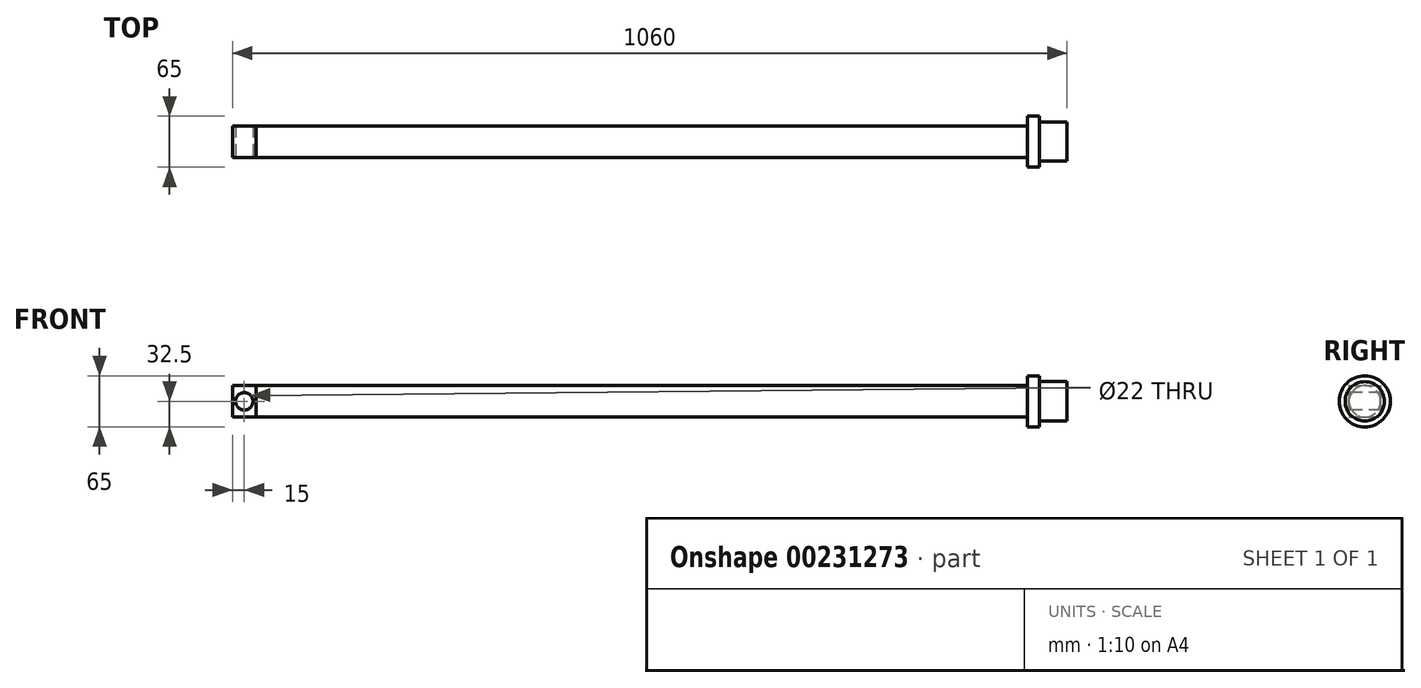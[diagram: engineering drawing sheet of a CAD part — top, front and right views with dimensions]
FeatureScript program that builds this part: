
annotation { "Feature Type Name" : "Feature", "Feature Type Description" : "" }
export const myFeature = defineFeature(function(context is Context, id is Id, definition is map)
    precondition{}
    {
        {
            var Q0;
            Q0=qCreatedBy(makeId("Right.planeOp"),FACE);
            var sketch = newSketch(context, id + "F0", { "sketchPlane" : qUnion([Q0])});
            skCircle(sketch, "E0", {"center": v(0, 0) * mm, "radius": 20 * mm});
            skSolve(sketch);
        }
        {
            var Q0;
            Q0=makeQuery(id+"F0.imprint","IMPRINT",FACE,{"disambiguationData":[TD([[makeQuery(id+"F0.imprint","IMPRINT",EDGE,{"derivedFrom":sQuery(id+"F0.wireOp",EDGE,"E0")}),1.0]])]});
            extrude(context, id + "F1", {"entities" : qUnion([Q0]), "endBound" : BoundingType.SYMMETRIC, "depth" : 1010 * mm});
        }
        {
            var Q0;
            Q0=makeQuery(id+"F1.opExtrude","CAP_FACE",FACE,{"disambiguationData":[OSD([sQuery(id+"F0.wireOp",EDGE,"E0")])],"isStart":false});
            var sketch = newSketch(context, id + "F2", { "sketchPlane" : qUnion([Q0])});
            skCircle(sketch, "E1", {"center": v(0, 0) * mm, "radius": 32.5 * mm});
            skCircle(sketch, "E2", {"center": v(0, 0) * mm, "radius": 25 * mm});
            skSolve(sketch);
        }
        {
            var Q0;
            Q0=makeQuery(id+"F2.imprint","IMPRINT",FACE,{"disambiguationData":[TD([[makeQuery(id+"F2.imprint","IMPRINT",EDGE,{"derivedFrom":sQuery(id+"F2.wireOp",EDGE,"E2")}),1.0]])]});
            var Q1;
            Q1=makeQuery(id+"F1.opExtrude","CAP_FACE",FACE,{"disambiguationData":[OSD([sQuery(id+"F0.wireOp",EDGE,"E0")])],"isStart":false});
            extrude(context, id + "F3", {"entities" : qUnion([Q0, Q1]), "operationType" : NewBodyOperationType.ADD, "depth" : 50 * mm});
        }
        {
            var Q0;
            Q0=makeQuery(id+"F2.imprint","IMPRINT",FACE,{"disambiguationData":[TD([[makeQuery(id+"F2.imprint","IMPRINT",EDGE,{"derivedFrom":sQuery(id+"F2.wireOp",EDGE,"E1")}),1.0]])]});
            extrude(context, id + "F4", {"entities" : qUnion([Q0]), "operationType" : NewBodyOperationType.ADD, "depth" : 15 * mm});
        }
        {
            var Q0;
            Q0=qCreatedBy(makeId("Front.planeOp"),FACE);
            var sketch = newSketch(context, id + "F5", { "sketchPlane" : qUnion([Q0])});
            skLineSegment(sketch, "E3", {"start": v(0, 0) * mm, "end": v(-517.62, 0) * mm, "construction": true});
            skLineSegment(sketch, "E4.0", {"start": v(-505, 20) * mm, "end": v(-505, -20) * mm, "construction": true});
            skCircle(sketch, "E5", {"center": v(-490, 0) * mm, "radius": 11 * mm});
            skSolve(sketch);
        }
        {
            var Q0;
            Q0=makeQuery(id+"F5.imprint","IMPRINT",FACE,{"disambiguationData":[TD([[makeQuery(id+"F5.imprint","IMPRINT",EDGE,{"derivedFrom":sQuery(id+"F5.wireOp",EDGE,"E5")}),1.0]])]});
            extrude(context, id + "F6", {"entities" : qUnion([Q0]), "operationType" : NewBodyOperationType.REMOVE, "endBound" : BoundingType.THROUGH_ALL, "oppositeDirection" : true, "depth" : 25 * mm, "hasSecondDirection" : true, "secondDirectionOppositeDirection" : false, "secondDirectionDepth" : 25 * mm});
        }
        {
            var Q0;
            Q0=makeQuery(id+"F1.opExtrude","CAP_FACE",FACE,{"disambiguationData":[OSD([sQuery(id+"F0.wireOp",EDGE,"E0")])],"isStart":true});
            var sketch = newSketch(context, id + "F7", { "sketchPlane" : qUnion([Q0])});
            skLineSegment(sketch, "E6.bottom", {"start": v(20, 20) * mm, "end": v(-20, 20) * mm});
            skLineSegment(sketch, "E6.top", {"start": v(20, -20) * mm, "end": v(-20, -20) * mm});
            skLineSegment(sketch, "E6.left", {"start": v(20, 20) * mm, "end": v(20, -20) * mm});
            skLineSegment(sketch, "E6.right", {"start": v(-20, 20) * mm, "end": v(-20, -20) * mm});
            skPoint(sketch, "E6.middle", {"position": v(0, 0) * mm});
            skCircle(sketch, "E7.0.0", {"center": v(0, 0) * mm, "radius": 20 * mm});
            skSolve(sketch);
        }
        {
            var Q0;
            {var subQ0=sQuery(id+"F7.wireOp",EDGE,"E6.right");var subQ1=sQuery(id+"F7.wireOp",EDGE,"E6.bottom");var subQ2=makeQuery(id+"F7.imprint","INTERSECT",VERTEX,{"derivedFrom":[subQ1,subQ0]});Q0=makeQuery(id+"F7.imprint","IMPRINT",FACE,{"disambiguationData":[TD([[makeQuery(id+"F7.imprint","IMPRINT",EDGE,{"disambiguationData":[TD([[subQ2,1.0]])],"derivedFrom":subQ1}),1.0]])]});}
            var Q1;
            {var subQ0=sQuery(id+"F7.wireOp",EDGE,"E6.right");var subQ1=sQuery(id+"F7.wireOp",EDGE,"E6.top");var subQ2=makeQuery(id+"F7.imprint","INTERSECT",VERTEX,{"derivedFrom":[subQ1,subQ0]});Q1=makeQuery(id+"F7.imprint","IMPRINT",FACE,{"disambiguationData":[TD([[makeQuery(id+"F7.imprint","IMPRINT",EDGE,{"disambiguationData":[TD([[subQ2,1.0]])],"derivedFrom":subQ1}),-1.0]])]});}
            var Q2;
            {var subQ0=sQuery(id+"F7.wireOp",EDGE,"E6.left");var subQ1=sQuery(id+"F7.wireOp",EDGE,"E6.top");var subQ2=makeQuery(id+"F7.imprint","INTERSECT",VERTEX,{"derivedFrom":[subQ1,subQ0]});Q2=makeQuery(id+"F7.imprint","IMPRINT",FACE,{"disambiguationData":[TD([[makeQuery(id+"F7.imprint","IMPRINT",EDGE,{"disambiguationData":[TD([[subQ2,-1.0]])],"derivedFrom":subQ1}),-1.0]])]});}
            var Q3;
            {var subQ0=sQuery(id+"F7.wireOp",EDGE,"E6.left");var subQ1=sQuery(id+"F7.wireOp",EDGE,"E6.bottom");var subQ2=makeQuery(id+"F7.imprint","INTERSECT",VERTEX,{"derivedFrom":[subQ1,subQ0]});Q3=makeQuery(id+"F7.imprint","IMPRINT",FACE,{"disambiguationData":[TD([[makeQuery(id+"F7.imprint","IMPRINT",EDGE,{"disambiguationData":[TD([[subQ2,-1.0]])],"derivedFrom":subQ1}),1.0]])]});}
            var Q4;
            {var subQ0=sQuery(id+"F7.wireOp",EDGE,"E7.0.0");var subQ1=makeQuery(id+"F7.imprint","INTERSECT",VERTEX,{"derivedFrom":[sQuery(id+"F7.wireOp",EDGE,"E6.bottom"),subQ0]});Q4=makeQuery(id+"F7.imprint","IMPRINT",FACE,{"disambiguationData":[TD([[makeQuery(id+"F7.imprint","IMPRINT",EDGE,{"disambiguationData":[TD([[subQ1,1.0]])],"derivedFrom":subQ0}),-1.0]])]});}
            extrude(context, id + "F8", {"entities" : qUnion([Q0, Q1, Q2, Q3, Q4]), "operationType" : NewBodyOperationType.ADD, "oppositeDirection" : true, "depth" : 30 * mm});
        }
        {
            var Q0;
            Q0=makeQuery(id+"F8.opExtrude","SWEPT_FACE",FACE,{"disambiguationData":[OSD([sQuery(id+"F7.wireOp",EDGE,"E6.left")])]});
            var sketch = newSketch(context, id + "F9", { "sketchPlane" : qUnion([Q0])});
            skCircle(sketch, "E8.0", {"center": v(-490, 0) * mm, "radius": 11 * mm});
            skSolve(sketch);
        }
        {
            var Q0;
            Q0=makeQuery(id+"F9.imprint","IMPRINT",FACE,{"disambiguationData":[TD([[makeQuery(id+"F9.imprint","IMPRINT",EDGE,{"derivedFrom":sQuery(id+"F9.wireOp",EDGE,"E8.0")}),1.0]])]});
            extrude(context, id + "F10", {"entities" : qUnion([Q0]), "operationType" : NewBodyOperationType.REMOVE, "endBound" : BoundingType.THROUGH_ALL, "oppositeDirection" : true, "depth" : 25 * mm});
        }
    });
